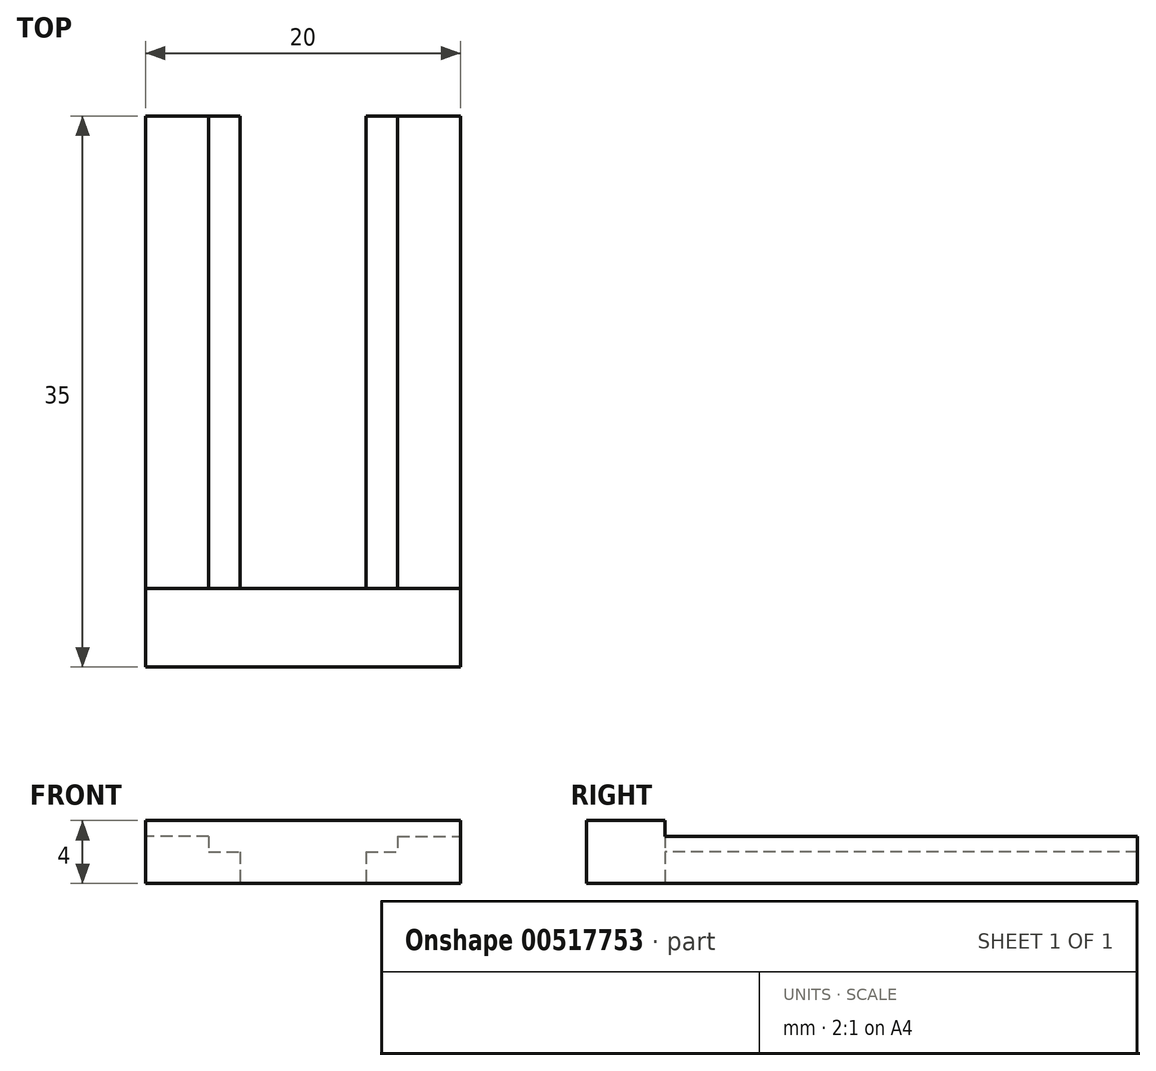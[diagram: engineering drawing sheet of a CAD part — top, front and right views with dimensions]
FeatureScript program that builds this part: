
annotation { "Feature Type Name" : "Feature", "Feature Type Description" : "" }
export const myFeature = defineFeature(function(context is Context, id is Id, definition is map)
    precondition{}
    {
        {
            var Q0;
            Q0=qCreatedBy(makeId("Top.planeOp"),FACE);
            var sketch = newSketch(context, id + "F0", { "sketchPlane" : qUnion([Q0])});
            skLineSegment(sketch, "E0.bottom", {"start": v(-27.5, 21.69) * mm, "end": v(-17.01, 21.69) * mm});
            skLineSegment(sketch, "E0.top", {"start": v(-27.5, 10.06) * mm, "end": v(-17.01, 10.06) * mm});
            skLineSegment(sketch, "E0.left", {"start": v(-27.5, 21.69) * mm, "end": v(-27.5, 10.06) * mm});
            skLineSegment(sketch, "E0.right", {"start": v(-17.01, 21.69) * mm, "end": v(-17.01, 10.06) * mm});
            skLineSegment(sketch, "E1.bottom", {"start": v(-10, 35) * mm, "end": v(10, 35) * mm});
            skLineSegment(sketch, "E1.top", {"start": v(-10, 0) * mm, "end": v(10, 0) * mm});
            skLineSegment(sketch, "E1.left", {"start": v(-10, 35) * mm, "end": v(-10, 0) * mm});
            skLineSegment(sketch, "E1.right", {"start": v(10, 35) * mm, "end": v(10, 0) * mm});
            skPoint(sketch, "E2", {"position": v(0, 35) * mm});
            skLineSegment(sketch, "E3.bottom", {"start": v(-6, 35) * mm, "end": v(6, 35) * mm});
            skLineSegment(sketch, "E3.top", {"start": v(-6, 5) * mm, "end": v(6, 5) * mm});
            skLineSegment(sketch, "E3.left", {"start": v(-6, 35) * mm, "end": v(-6, 5) * mm});
            skLineSegment(sketch, "E3.right", {"start": v(6, 35) * mm, "end": v(6, 5) * mm});
            skLineSegment(sketch, "E4.bottom", {"start": v(-4, 35) * mm, "end": v(4, 35) * mm});
            skLineSegment(sketch, "E4.top", {"start": v(-4, 5) * mm, "end": v(4, 5) * mm});
            skLineSegment(sketch, "E4.left", {"start": v(-4, 35) * mm, "end": v(-4, 5) * mm});
            skLineSegment(sketch, "E4.right", {"start": v(4, 35) * mm, "end": v(4, 5) * mm});
            skLineSegment(sketch, "E5", {"start": v(-6, 5) * mm, "end": v(-10, 5) * mm});
            skLineSegment(sketch, "E6", {"start": v(6, 5) * mm, "end": v(10, 5) * mm});
            skSolve(sketch);
        }
        {
            var Q0;
            Q0=makeQuery(id+"F0.imprint","IMPRINT",FACE,{"disambiguationData":[TD([[makeQuery(id+"F0.imprint","IMPRINT",EDGE,{"derivedFrom":sQuery(id+"F0.wireOp",EDGE,"E1.top")}),1.0]])]});
            extrude(context, id + "F1", {"entities" : qUnion([Q0]), "depth" : 4 * mm, "offsetDistance" : 25 * mm});
        }
        {
            var Q0;
            {var subQ0=sQuery(id+"F0.wireOp",EDGE,"E3.left");Q0=makeQuery(id+"F0.imprint","IMPRINT",FACE,{"disambiguationData":[TD([[makeQuery(id+"F0.imprint","IMPRINT",EDGE,{"derivedFrom":subQ0}),1.0]])]});}
            var Q1;
            {var subQ0=sQuery(id+"F0.wireOp",EDGE,"E3.right");Q1=makeQuery(id+"F0.imprint","IMPRINT",FACE,{"disambiguationData":[TD([[makeQuery(id+"F0.imprint","IMPRINT",EDGE,{"derivedFrom":subQ0}),-1.0]])]});}
            extrude(context, id + "F2", {"entities" : qUnion([Q0, Q1]), "operationType" : NewBodyOperationType.ADD, "depth" : 2 * mm, "offsetDistance" : 25 * mm});
        }
        {
            var Q0;
            {var subQ3=sQuery(id+"F0.wireOp",EDGE,"E3.right");Q0=makeQuery(id+"F0.imprint","IMPRINT",FACE,{"disambiguationData":[TD([[makeQuery(id+"F0.imprint","IMPRINT",EDGE,{"derivedFrom":subQ3}),1.0]])]});}
            var Q1;
            {var subQ3=sQuery(id+"F0.wireOp",EDGE,"E3.left");Q1=makeQuery(id+"F0.imprint","IMPRINT",FACE,{"disambiguationData":[TD([[makeQuery(id+"F0.imprint","IMPRINT",EDGE,{"derivedFrom":subQ3}),-1.0]])]});}
            extrude(context, id + "F3", {"entities" : qUnion([Q0, Q1]), "operationType" : NewBodyOperationType.ADD, "depth" : 3 * mm, "offsetDistance" : 25 * mm});
        }
    });
